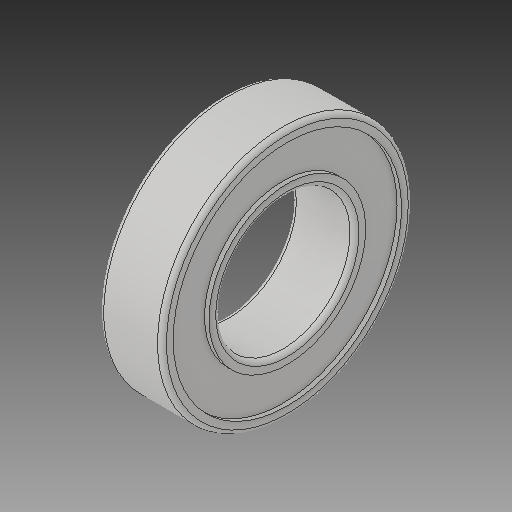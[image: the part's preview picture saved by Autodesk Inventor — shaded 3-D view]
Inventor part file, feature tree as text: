
AUTODESK INVENTOR PART (.ipt)
format: ipt  version: 2018 (Build 220112000, 112)  size: 176,128 bytes
history: native  units: in
note: dims shown in document units (in); Inventor stores cm internally (conversion verified against a paired STEP export)
features: fillet x1
ambient origin geometry x8: Origin, YZ Plane, XZ Plane, XY Plane, X Axis, Y Axis, Z Axis, Center Point
bodies: Solid1 (feature_tree)
feature tree (1):
  fillet  "Fillet1"  [1 undecoded]
note: 1 required parameter value undecoded (feature->parameter linkage not recoverable at this tier; creation-order binding heuristic only, values carry confidence <= 0.55)
